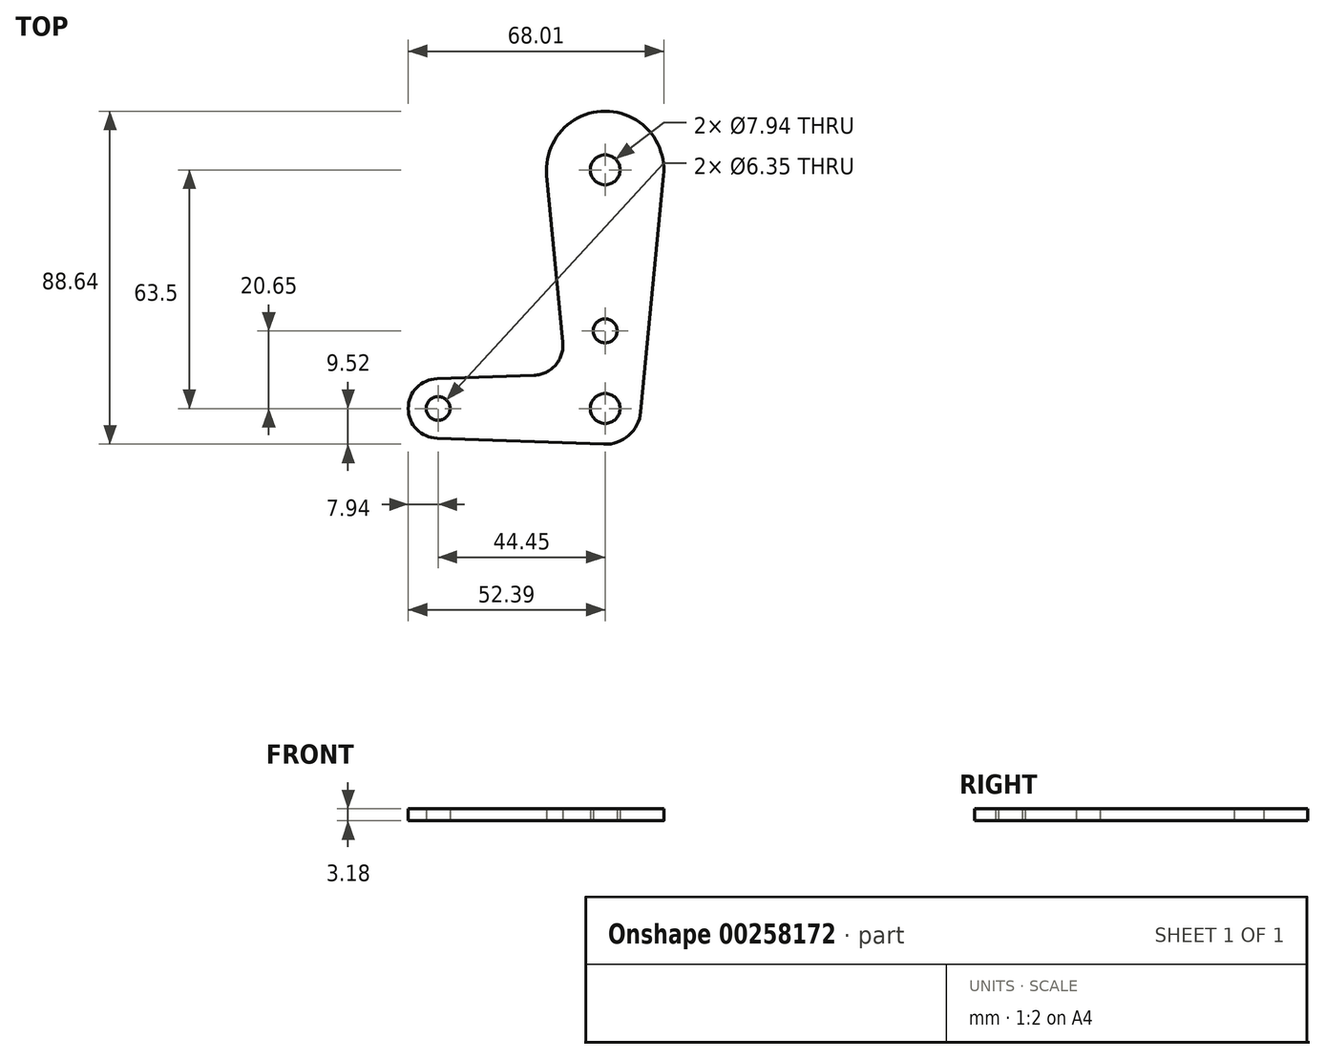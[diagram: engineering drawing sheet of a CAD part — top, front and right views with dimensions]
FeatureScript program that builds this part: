
annotation { "Feature Type Name" : "Feature", "Feature Type Description" : "" }
export const myFeature = defineFeature(function(context is Context, id is Id, definition is map)
    precondition{}
    {
        {
            var Q0;
            Q0=qCreatedBy(makeId("Top.planeOp"),FACE);
            var sketch = newSketch(context, id + "F0", { "sketchPlane" : qUnion([Q0])});
            skCircle(sketch, "E0", {"center": v(0, 0) * mm, "radius": 3.97 * mm});
            skLineSegment(sketch, "E1", {"start": v(0, 0) * mm, "end": v(-44.45, 0) * mm, "construction": true});
            skCircle(sketch, "E2", {"center": v(-44.45, 0) * mm, "radius": 3.18 * mm});
            skCircle(sketch, "E3", {"center": v(-44.45, 0) * mm, "radius": 7.94 * mm});
            skLineSegment(sketch, "E4", {"start": v(0, 0) * mm, "end": v(0, 63.5) * mm, "construction": true});
            skCircle(sketch, "E5", {"center": v(0, 63.5) * mm, "radius": 3.97 * mm});
            skCircle(sketch, "E6", {"center": v(0, 63.5) * mm, "radius": 15.62 * mm});
            skCircle(sketch, "E7", {"center": v(0, 0) * mm, "radius": 9.53 * mm});
            skLineSegment(sketch, "E8", {"start": v(0, 0) * mm, "end": v(0, 20.65) * mm, "construction": true});
            skCircle(sketch, "E9", {"center": v(0, 20.65) * mm, "radius": 3.18 * mm});
            skLineSegment(sketch, "E10", {"start": v(15.55, 62) * mm, "end": v(9.48, -0.91) * mm});
            skLineSegment(sketch, "E11", {"start": v(-15.55, 62) * mm, "end": v(-9.48, -0.91) * mm});
            skLineSegment(sketch, "E12", {"start": v(-44.73, 7.93) * mm, "end": v(0, 9.53) * mm});
            skLineSegment(sketch, "E13", {"start": v(-44.73, -7.93) * mm, "end": v(-0.34, -9.52) * mm});
            skSolve(sketch);
        }
        {
            var Q0;
            Q0 = qSketchRegion(id + "F0", true);
            extrude(context, id + "F1", {"entities" : qUnion([Q0]), "depth" : 3.17 * mm});
        }
        {
            var Q0;
            Q0=makeQuery(id+"F1.opExtrude","SWEPT_EDGE",EDGE,{"disambiguationData":[OSD([sQuery(id+"F0.wireOp",EDGE,"E11"),sQuery(id+"F0.wireOp",EDGE,"E12")])]});
            fillet(context, id + "F2", {"entities" : qUnion([Q0]), "radius" : 7.94 * mm, "tangentPropagation" : true, "allowEdgeOverflow" : false});
        }
    });
